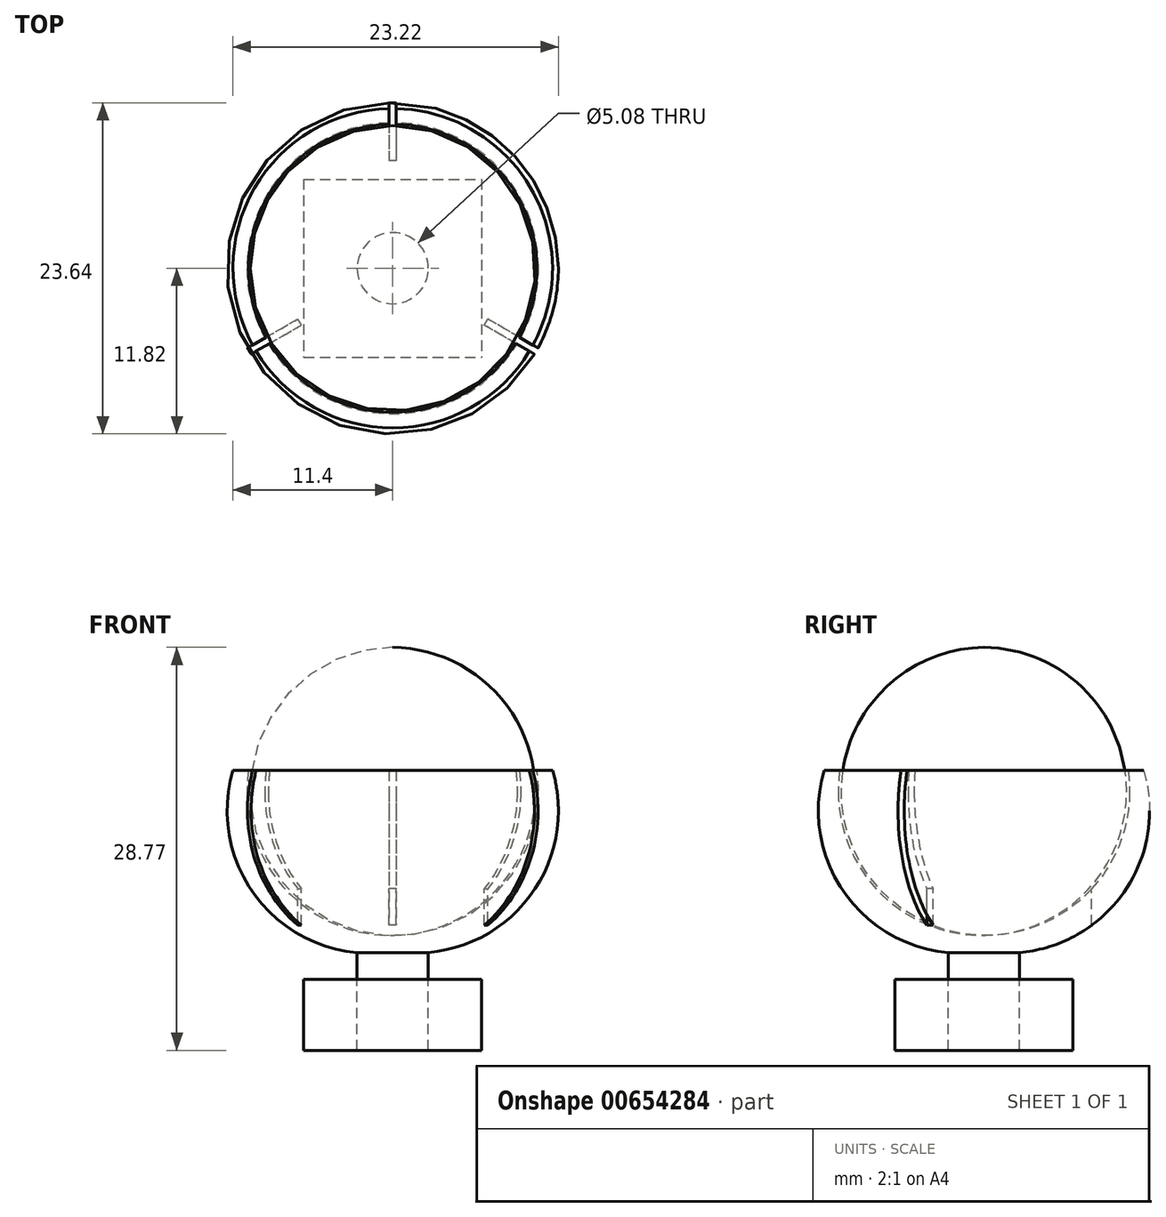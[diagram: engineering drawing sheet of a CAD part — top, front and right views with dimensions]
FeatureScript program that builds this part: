
annotation { "Feature Type Name" : "Feature", "Feature Type Description" : "" }
export const myFeature = defineFeature(function(context is Context, id is Id, definition is map)
    precondition{}
    {
        {
            var Q0;
            Q0=qCreatedBy(makeId("Front.planeOp"),FACE);
            var sketch = newSketch(context, id + "F0", { "sketchPlane" : qUnion([Q0])});
            skArc(sketch, "E0", {"start": v(-10.29, 11.79) * mm, "mid": v(-7.86, 3.52) * mm, "end": v(0, 0) * mm});
            skLineSegment(sketch, "E1", {"start": v(-10.29, 11.79) * mm, "end": v(-11.4, 11.79) * mm});
            skLineSegment(sketch, "E2", {"start": v(0, 0) * mm, "end": v(0, -1.12) * mm});
            skArc(sketch, "E3", {"start": v(-11.4, 11.79) * mm, "mid": v(-9.27, 2.18) * mm, "end": v(0, -1.12) * mm});
            skLineSegment(sketch, "E4", {"start": v(-2.54, -1.22) * mm, "end": v(-2.54, -3.12) * mm});
            skLineSegment(sketch, "E5", {"start": v(-2.54, -3.12) * mm, "end": v(0, -3.12) * mm});
            skLineSegment(sketch, "E6", {"start": v(0, -1.12) * mm, "end": v(0, -3.12) * mm});
            skSolve(sketch);
        }
        {
            var Q0;
            Q0=makeQuery(id+"F0.imprint","IMPRINT",FACE,{"disambiguationData":[TD([[makeQuery(id+"F0.imprint","IMPRINT",EDGE,{"derivedFrom":sQuery(id+"F0.wireOp",EDGE,"E0")}),-1.0]])]});
            var Q1;
            {var subQ2=sQuery(id+"F0.wireOp",EDGE,"E4");Q1=makeQuery(id+"F0.imprint","IMPRINT",FACE,{"disambiguationData":[TD([[makeQuery(id+"F0.imprint","IMPRINT",EDGE,{"derivedFrom":subQ2}),1.0]])]});}
            var Q2;
            Q2=sQuery(id+"F0.wireOp",EDGE,"E2");
            revolve(context, id + "F1", {"entities" : qUnion([Q0, Q1]), "axis" : qUnion([Q2]), "revolveType" : RevolveType.FULL});
        }
        {
            var Q0;
            Q0=makeQuery(id+"F1.opRevolve","SWEPT_FACE",FACE,{"disambiguationData":[OSD([sQuery(id+"F0.wireOp",EDGE,"E1")])]});
            var sketch = newSketch(context, id + "F2", { "sketchPlane" : qUnion([Q0])});
            skLineSegment(sketch, "E7.bottom", {"start": v(-0.25, 7.69) * mm, "end": v(0.25, 7.69) * mm});
            skLineSegment(sketch, "E7.top", {"start": v(-0.25, 13.02) * mm, "end": v(0.25, 13.02) * mm});
            skLineSegment(sketch, "E7.left", {"start": v(-0.25, 7.69) * mm, "end": v(-0.25, 13.02) * mm});
            skLineSegment(sketch, "E7.right", {"start": v(0.25, 7.69) * mm, "end": v(0.25, 13.02) * mm});
            skLineSegment(sketch, "E8.1.0", {"start": v(-6.53, -4.06) * mm, "end": v(-11.15, -6.73) * mm});
            skLineSegment(sketch, "E8.1.1", {"start": v(-6.79, -3.62) * mm, "end": v(-11.4, -6.3) * mm});
            skLineSegment(sketch, "E8.1.2", {"start": v(-11.15, -6.73) * mm, "end": v(-11.4, -6.3) * mm});
            skLineSegment(sketch, "E8.1.3", {"start": v(-6.53, -4.06) * mm, "end": v(-6.79, -3.62) * mm});
            skLineSegment(sketch, "E8.2.0", {"start": v(6.79, -3.62) * mm, "end": v(11.4, -6.3) * mm});
            skLineSegment(sketch, "E8.2.1", {"start": v(6.53, -4.06) * mm, "end": v(11.15, -6.73) * mm});
            skLineSegment(sketch, "E8.2.2", {"start": v(11.4, -6.3) * mm, "end": v(11.15, -6.73) * mm});
            skLineSegment(sketch, "E8.2.3", {"start": v(6.79, -3.62) * mm, "end": v(6.53, -4.06) * mm});
            skPoint(sketch, "E8.center", {"position": v(0, 0) * mm});
            skSolve(sketch);
        }
        {
            var Q0;
            {var subQ0=sQuery(id+"F2.wireOp",EDGE,"E8.1.2");Q0=makeQuery(id+"F2.imprint","IMPRINT",FACE,{"disambiguationData":[TD([[makeQuery(id+"F2.imprint","IMPRINT",EDGE,{"derivedFrom":subQ0}),-1.0]])]});}
            var Q1;
            {var subQ0=sQuery(id+"F2.wireOp",EDGE,"E8.1.3");Q1=makeQuery(id+"F2.imprint","IMPRINT",FACE,{"disambiguationData":[TD([[makeQuery(id+"F2.imprint","IMPRINT",EDGE,{"derivedFrom":subQ0}),1.0]])]});}
            var Q2;
            {var subQ0=sQuery(id+"F2.wireOp",EDGE,"E8.1.0");var subQ1=sQuery(id+"F0.wireOp",EDGE,"E1");var subQ2=makeQuery(id+"F1.opRevolve","SWEPT_EDGE",EDGE,{"disambiguationData":[OSD([subQ1,sQuery(id+"F0.wireOp",EDGE,"E3")])]});var subQ3=makeQuery(id+"F2.imprint","INTERSECT",VERTEX,{"derivedFrom":[subQ2,subQ0]});Q2=makeQuery(id+"F2.imprint","IMPRINT",FACE,{"disambiguationData":[TD([[makeQuery(id+"F2.imprint","IMPRINT",EDGE,{"disambiguationData":[TD([[subQ3,1.0]])],"derivedFrom":subQ0}),-1.0]])]});}
            var Q3;
            {var subQ0=sQuery(id+"F2.wireOp",EDGE,"E7.top");Q3=makeQuery(id+"F2.imprint","IMPRINT",FACE,{"disambiguationData":[TD([[makeQuery(id+"F2.imprint","IMPRINT",EDGE,{"derivedFrom":subQ0}),-1.0]])]});}
            var Q4;
            {var subQ0=sQuery(id+"F2.wireOp",EDGE,"E7.left");var subQ1=sQuery(id+"F0.wireOp",EDGE,"E1");var subQ2=makeQuery(id+"F1.opRevolve","SWEPT_EDGE",EDGE,{"disambiguationData":[OSD([subQ1,sQuery(id+"F0.wireOp",EDGE,"E3")])]});var subQ3=makeQuery(id+"F2.imprint","INTERSECT",VERTEX,{"derivedFrom":[subQ2,subQ0]});Q4=makeQuery(id+"F2.imprint","IMPRINT",FACE,{"disambiguationData":[TD([[makeQuery(id+"F2.imprint","IMPRINT",EDGE,{"disambiguationData":[TD([[subQ3,1.0]])],"derivedFrom":subQ0}),-1.0]])]});}
            var Q5;
            {var subQ0=sQuery(id+"F2.wireOp",EDGE,"E7.bottom");Q5=makeQuery(id+"F2.imprint","IMPRINT",FACE,{"disambiguationData":[TD([[makeQuery(id+"F2.imprint","IMPRINT",EDGE,{"derivedFrom":subQ0}),1.0]])]});}
            var Q6;
            {var subQ0=sQuery(id+"F2.wireOp",EDGE,"E8.2.2");Q6=makeQuery(id+"F2.imprint","IMPRINT",FACE,{"disambiguationData":[TD([[makeQuery(id+"F2.imprint","IMPRINT",EDGE,{"derivedFrom":subQ0}),-1.0]])]});}
            var Q7;
            {var subQ0=sQuery(id+"F2.wireOp",EDGE,"E8.2.0");var subQ1=sQuery(id+"F0.wireOp",EDGE,"E1");var subQ2=makeQuery(id+"F1.opRevolve","SWEPT_EDGE",EDGE,{"disambiguationData":[OSD([subQ1,sQuery(id+"F0.wireOp",EDGE,"E3")])]});var subQ3=makeQuery(id+"F2.imprint","INTERSECT",VERTEX,{"derivedFrom":[subQ2,subQ0]});Q7=makeQuery(id+"F2.imprint","IMPRINT",FACE,{"disambiguationData":[TD([[makeQuery(id+"F2.imprint","IMPRINT",EDGE,{"disambiguationData":[TD([[subQ3,1.0]])],"derivedFrom":subQ0}),-1.0]])]});}
            var Q8;
            {var subQ0=sQuery(id+"F2.wireOp",EDGE,"E8.2.3");Q8=makeQuery(id+"F2.imprint","IMPRINT",FACE,{"disambiguationData":[TD([[makeQuery(id+"F2.imprint","IMPRINT",EDGE,{"derivedFrom":subQ0}),1.0]])]});}
            extrude(context, id + "F3", {"entities" : qUnion([Q0, Q1, Q2, Q3, Q4, Q5, Q6, Q7, Q8]), "operationType" : NewBodyOperationType.REMOVE, "oppositeDirection" : true, "depth" : 25.4 * mm, "offsetDistance" : 25.4 * mm});
        }
        {
            var Q0;
            Q0=makeQuery(id+"F1.opRevolve","SWEPT_FACE",FACE,{"disambiguationData":[OSD([sQuery(id+"F0.wireOp",EDGE,"E5")])]});
            var sketch = newSketch(context, id + "F4", { "sketchPlane" : qUnion([Q0])});
            skLineSegment(sketch, "E9.bottom", {"start": v(-6.35, -6.35) * mm, "end": v(6.35, -6.35) * mm});
            skLineSegment(sketch, "E9.top", {"start": v(-6.35, 6.35) * mm, "end": v(6.35, 6.35) * mm});
            skLineSegment(sketch, "E9.left", {"start": v(-6.35, -6.35) * mm, "end": v(-6.35, 6.35) * mm});
            skLineSegment(sketch, "E9.right", {"start": v(6.35, -6.35) * mm, "end": v(6.35, 6.35) * mm});
            skSolve(sketch);
        }
        {
            var Q0;
            Q0=makeQuery(id+"F4.imprint","IMPRINT",FACE,{"disambiguationData":[TD([[makeQuery(id+"F4.imprint","IMPRINT",EDGE,{"derivedFrom":sQuery(id+"F4.wireOp",EDGE,"E9.bottom")}),1.0]])]});
            extrude(context, id + "F5", {"entities" : qUnion([Q0]), "depth" : 5.08 * mm, "offsetDistance" : 25.4 * mm});
        }
    });
